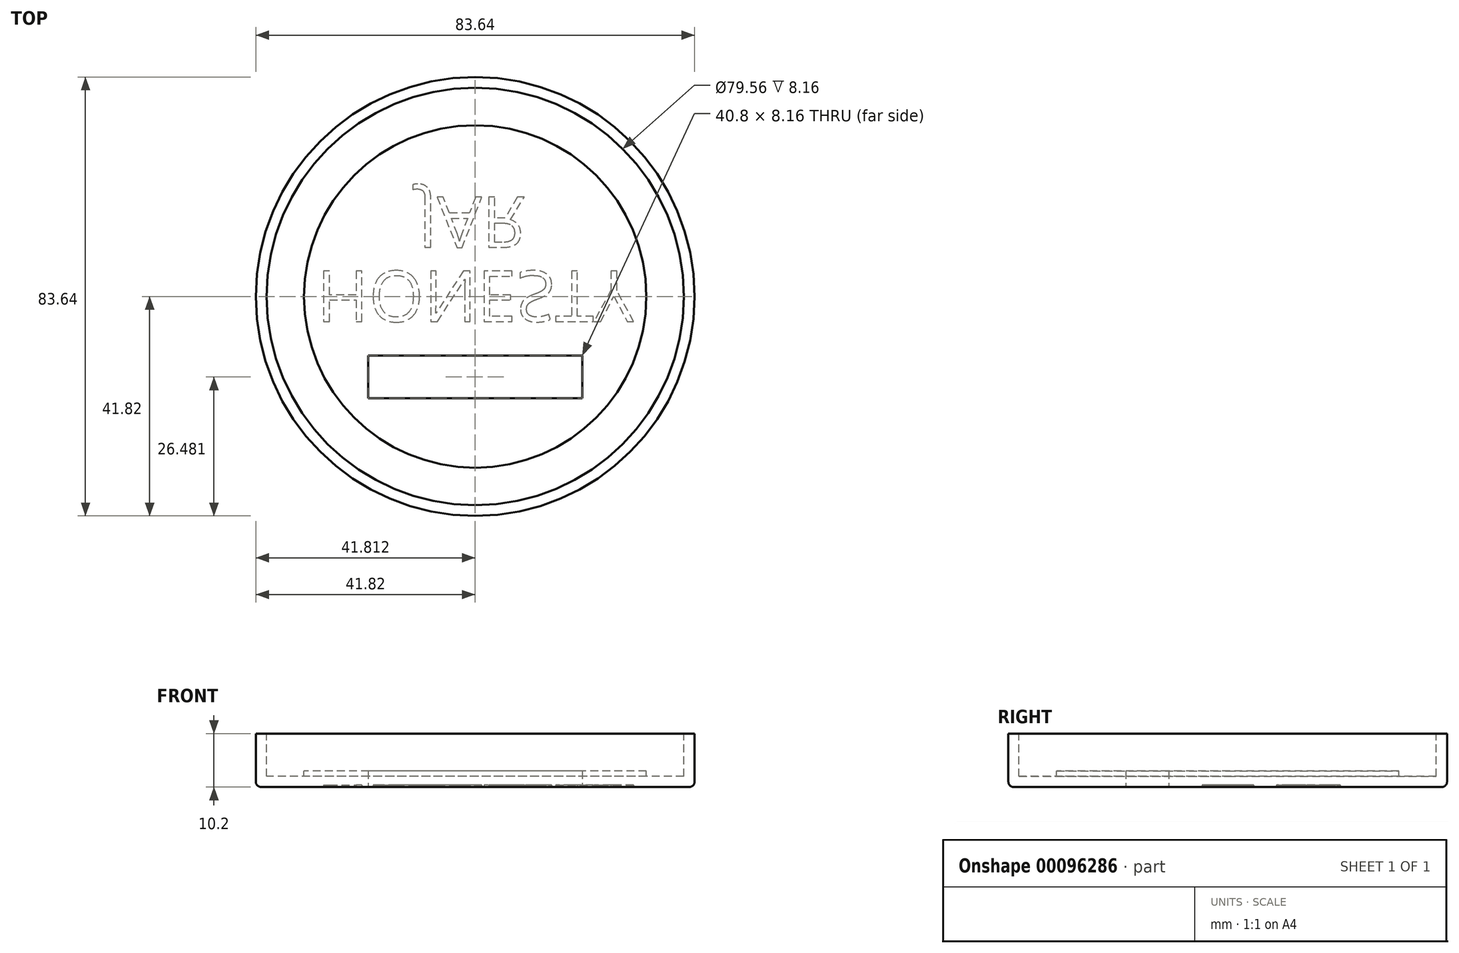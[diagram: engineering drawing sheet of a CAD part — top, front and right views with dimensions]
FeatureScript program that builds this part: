
annotation { "Feature Type Name" : "Feature", "Feature Type Description" : "" }
export const myFeature = defineFeature(function(context is Context, id is Id, definition is map)
    precondition{}
    {
        {
            var Q0;
            Q0=qCreatedBy(makeId("Top.planeOp"),FACE);
            var sketch = newSketch(context, id + "F0", { "sketchPlane" : qUnion([Q0])});
            skCircle(sketch, "E0", {"center": v(0, 0) * mm, "radius": 41 * mm});
            skSolve(sketch);
        }
        {
            var Q0;
            Q0=makeQuery(id+"F0.imprint","IMPRINT",FACE,{"disambiguationData":[TD([[makeQuery(id+"F0.imprint","IMPRINT",EDGE,{"derivedFrom":sQuery(id+"F0.wireOp",EDGE,"E0")}),1.0]])]});
            extrude(context, id + "F1", {"entities" : qUnion([Q0]), "depth" : 10 * mm});
        }
        {
            var Q0;
            Q0=makeQuery(id+"F1.opExtrude","CAP_FACE",FACE,{"disambiguationData":[OSD([sQuery(id+"F0.wireOp",EDGE,"E0")])],"isStart":false});
            var sketch = newSketch(context, id + "F2", { "sketchPlane" : qUnion([Q0])});
            skCircle(sketch, "E1", {"center": v(0, 0) * mm, "radius": 39 * mm});
            skCircle(sketch, "E2.0", {"center": v(0, 0) * mm, "radius": 32 * mm});
            skSolve(sketch);
        }
        {
            var Q0;
            Q0=makeQuery(id+"F2.imprint","IMPRINT",FACE,{"disambiguationData":[TD([[makeQuery(id+"F2.imprint","IMPRINT",EDGE,{"derivedFrom":sQuery(id+"F2.wireOp",EDGE,"E1")}),1.0]])]});
            extrude(context, id + "F3", {"entities" : qUnion([Q0]), "operationType" : NewBodyOperationType.REMOVE, "oppositeDirection" : true, "depth" : 8 * mm});
        }
        {
            var Q0;
            Q0=makeQuery(id+"F3.boolean.opBoolean","SPLIT",FACE,{"disambiguationData":[TD([makeQuery(id+"F3.opExtrude","SWEPT_FACE",FACE,{"disambiguationData":[OSD([sQuery(id+"F2.wireOp",EDGE,"E2.0")])]})])],"derivedFrom":makeQuery(id+"F1.opExtrude","CAP_FACE",FACE,{"disambiguationData":[OSD([sQuery(id+"F0.wireOp",EDGE,"E0")])],"isStart":false})});
            extrude(context, id + "F4", {"entities" : qUnion([Q0]), "operationType" : NewBodyOperationType.REMOVE, "oppositeDirection" : true, "depth" : 7 * mm});
        }
        {
            var Q0;
            Q0=makeQuery(id+"F1.opExtrude","CAP_FACE",FACE,{"disambiguationData":[OSD([sQuery(id+"F0.wireOp",EDGE,"E0")])],"isStart":true});
            var sketch = newSketch(context, id + "F5", { "sketchPlane" : qUnion([Q0])});
            skCircle(sketch, "E3", {"center": v(0, 0) * mm, "radius": 30 * mm, "construction": true});
            skText(sketch, "E4", { "text": "HONESTY", "fontName": "OpenSans-Regular.ttf"});
            skPoint(sketch, "E5", {"position": v(-50.04, -9.08) * mm});
            skPoint(sketch, "E6.MirrorP", {"position": v(49.96, -9.08) * mm});
            skLineSegment(sketch, "E7", {"start": v(-50.04, -9.08) * mm, "end": v(49.96, -9.08) * mm, "construction": true});
            skLineSegment(sketch, "E8", {"start": v(-50.04, -18.57) * mm, "end": v(50.16, -18.57) * mm, "construction": true});
            skText(sketch, "E9", { "text": "JAR", "fontName": "OpenSans-Regular.ttf"});
            const initialGuessF5  = {"E4": [-0.02962, -0.00475, 1, 0, 0.0095], "E9": [-0.01063, -0.01857, 1, 0, 0.00949]};
            skSetInitialGuess(sketch, initialGuessF5);
            skSolve(sketch);
        }
        {
            var Q0;
            Q0 = qSketchRegion(id + "F5", true);
            extrude(context, id + "F6", {"entities" : qUnion([Q0]), "operationType" : NewBodyOperationType.REMOVE, "oppositeDirection" : true, "depth" : 0.4 * mm});
        }
        {
            var Q0;
            {var subQ0=sQuery(id+"F0.wireOp",EDGE,"E0");Q0=makeQuery(id+"F6.boolean.opBoolean","SPLIT",FACE,{"disambiguationData":[TD([makeQuery(id+"F1.opExtrude","SWEPT_FACE",FACE,{"disambiguationData":[OSD([subQ0])]})])],"derivedFrom":makeQuery(id+"F1.opExtrude","CAP_FACE",FACE,{"disambiguationData":[OSD([subQ0])],"isStart":true})});}
            var sketch = newSketch(context, id + "F7", { "sketchPlane" : qUnion([Q0])});
            skLineSegment(sketch, "E10.bottom", {"start": v(-20, 19.04) * mm, "end": v(20, 19.04) * mm});
            skLineSegment(sketch, "E10.top", {"start": v(-20, 11.04) * mm, "end": v(20, 11.04) * mm});
            skLineSegment(sketch, "E10.left", {"start": v(-20, 19.04) * mm, "end": v(-20, 11.04) * mm});
            skLineSegment(sketch, "E10.right", {"start": v(20, 19.04) * mm, "end": v(20, 11.04) * mm});
            skLineSegment(sketch, "E11", {"start": v(0, 0) * mm, "end": v(0, 41) * mm, "construction": true});
            skLineSegment(sketch, "E12", {"start": v(0, 41) * mm, "end": v(41, 0) * mm, "construction": true});
            skLineSegment(sketch, "E13", {"start": v(41, 0) * mm, "end": v(-41, 0) * mm, "construction": true});
            skLineSegment(sketch, "E14", {"start": v(-41, 0) * mm, "end": v(0, 41) * mm, "construction": true});
            skSolve(sketch);
        }
        {
            var Q0;
            Q0=makeQuery(id+"F7.imprint","IMPRINT",FACE,{"disambiguationData":[TD([[makeQuery(id+"F7.imprint","IMPRINT",EDGE,{"derivedFrom":sQuery(id+"F7.wireOp",EDGE,"E10.bottom")}),-1.0]])]});
            extrude(context, id + "F8", {"entities" : qUnion([Q0]), "operationType" : NewBodyOperationType.REMOVE, "oppositeDirection" : true, "depth" : 25 * mm});
        }
        {
            var Q0;
            Q0=makeQuery(id+"F1.opExtrude","CAP_EDGE",EDGE,{"disambiguationData":[OSD([sQuery(id+"F0.wireOp",EDGE,"E0")])],"isStart":true});
            var Q1;
            Q1=makeQuery(id+"F8.boolean.opBoolean","COPY",EDGE,{"derivedFrom":makeQuery(id+"F8.opExtrude","CAP_EDGE",EDGE,{"disambiguationData":[OSD([sQuery(id+"F7.wireOp",EDGE,"E10.bottom")])],"isStart":true})});
            var Q2;
            Q2=makeQuery(id+"F8.boolean.opBoolean","COPY",EDGE,{"derivedFrom":makeQuery(id+"F8.opExtrude","CAP_EDGE",EDGE,{"disambiguationData":[OSD([sQuery(id+"F7.wireOp",EDGE,"E10.left")])],"isStart":true})});
            var Q3;
            Q3=makeQuery(id+"F8.boolean.opBoolean","COPY",EDGE,{"derivedFrom":makeQuery(id+"F8.opExtrude","CAP_EDGE",EDGE,{"disambiguationData":[OSD([sQuery(id+"F7.wireOp",EDGE,"E10.top")])],"isStart":true})});
            var Q4;
            Q4=makeQuery(id+"F8.boolean.opBoolean","COPY",EDGE,{"derivedFrom":makeQuery(id+"F8.opExtrude","CAP_EDGE",EDGE,{"disambiguationData":[OSD([sQuery(id+"F7.wireOp",EDGE,"E10.right")])],"isStart":true})});
            var Q5;
            Q5=makeQuery(id+"F4.boolean.opBoolean","COPY",EDGE,{"derivedFrom":makeQuery(id+"F4.opExtrude","CAP_EDGE",EDGE,{"disambiguationData":[OSD([sQuery(id+"F2.wireOp",EDGE,"E2.0")])],"isStart":false})});
            fillet(context, id + "F9", {"entities" : qUnion([Q0, Q1, Q2, Q3, Q4, Q5]), "radius" : 1 * mm, "tangentPropagation" : true, "allowEdgeOverflow" : false});
        }
        {
            var Q0;
            Q0=makeQuery(id+"F1.opExtrude","SWEPT_BODY",BODY,{"disambiguationData":[OSD([sQuery(id+"F0.wireOp",EDGE,"E0")])]});
            var Q1;
            Q1=qCreatedBy(makeId("Origin.pointOp"),VERTEX);
            transform(context, id + "F10", {"entities" : qUnion([Q0]), "transformType" : TransformType.SCALE_UNIFORMLY, "scale" : 1.02, "scalePoint" : qUnion([Q1]), "makeCopy" : false});
        }
    });
